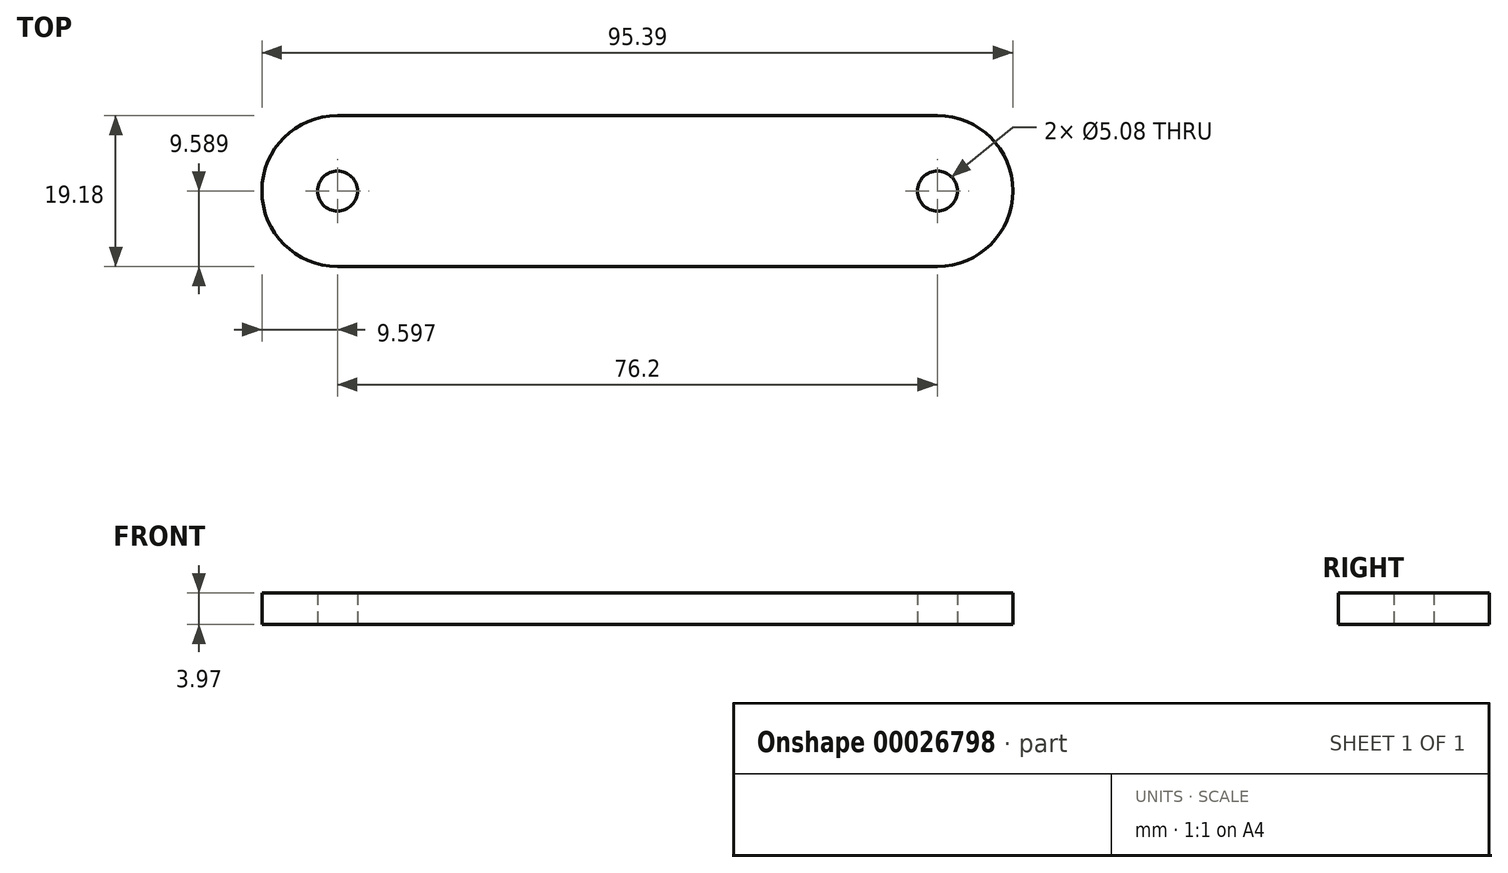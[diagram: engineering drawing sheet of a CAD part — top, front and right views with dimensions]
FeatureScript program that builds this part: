
annotation { "Feature Type Name" : "Feature", "Feature Type Description" : "" }
export const myFeature = defineFeature(function(context is Context, id is Id, definition is map)
    precondition{}
    {
        {
            var Q0;
            Q0=qCreatedBy(makeId("Top.planeOp"),FACE);
            var sketch = newSketch(context, id + "F0", { "sketchPlane" : qUnion([Q0])});
            skLineSegment(sketch, "E0.bottom", {"start": v(-20.57, 6.76) * mm, "end": v(55.63, 6.76) * mm});
            skLineSegment(sketch, "E0.top", {"start": v(-20.57, -12.42) * mm, "end": v(55.63, -12.42) * mm});
            skLineSegment(sketch, "E0.left", {"start": v(-20.57, -0.3) * mm, "end": v(-20.57, -5.37) * mm});
            skLineSegment(sketch, "E0.right", {"start": v(55.63, -0.3) * mm, "end": v(55.63, -5.37) * mm});
            skArc(sketch, "E1", {"start": v(-20.57, 6.76) * mm, "mid": v(-30.17, -2.83) * mm, "end": v(-20.57, -12.42) * mm});
            skArc(sketch, "E2", {"start": v(55.63, -12.42) * mm, "mid": v(65.22, -2.83) * mm, "end": v(55.63, 6.76) * mm});
            skCircle(sketch, "E3", {"center": v(55.63, -2.83) * mm, "radius": 2.54 * mm});
            skCircle(sketch, "E4", {"center": v(-20.57, -2.83) * mm, "radius": 2.54 * mm});
            skSolve(sketch);
        }
        {
            var Q0;
            Q0=makeQuery(id+"F0.imprint","IMPRINT",FACE,{"disambiguationData":[TD([[makeQuery(id+"F0.imprint","IMPRINT",EDGE,{"derivedFrom":sQuery(id+"F0.wireOp",EDGE,"E0.bottom")}),-1.0]])]});
            extrude(context, id + "F1", {"entities" : qUnion([Q0]), "depth" : 3.97 * mm});
        }
    });
